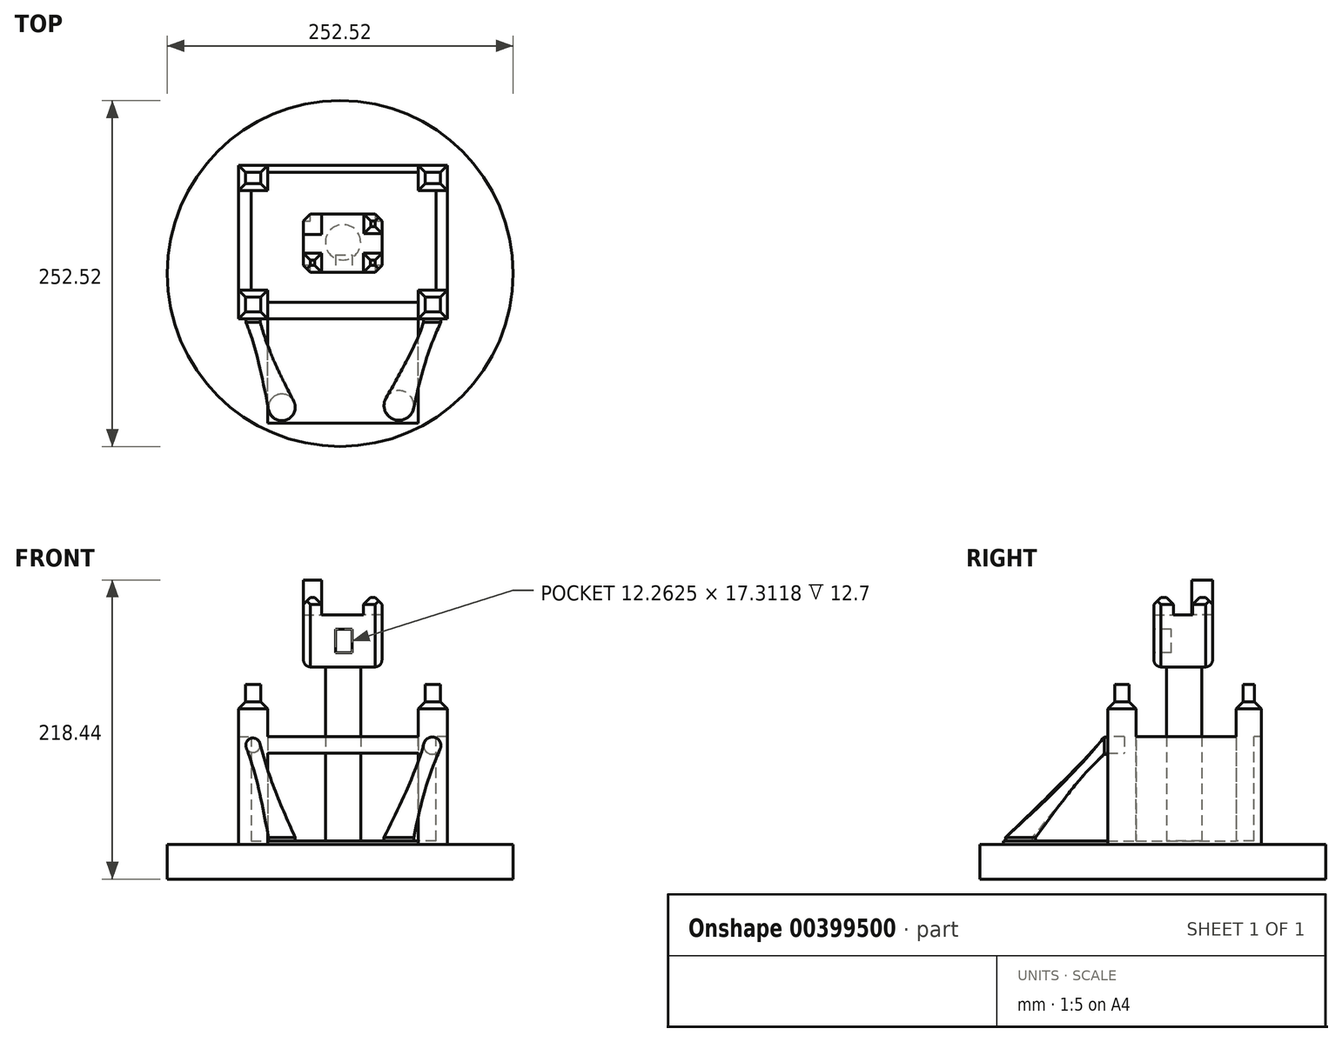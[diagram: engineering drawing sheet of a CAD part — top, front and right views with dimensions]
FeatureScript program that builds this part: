
annotation { "Feature Type Name" : "Feature", "Feature Type Description" : "" }
export const myFeature = defineFeature(function(context is Context, id is Id, definition is map)
    precondition{}
    {
        {
            var Q0;
            Q0=qCreatedBy(makeId("Top.planeOp"),FACE);
            var sketch = newSketch(context, id + "F0", { "sketchPlane" : qUnion([Q0])});
            skLineSegment(sketch, "E0.bottom", {"start": v(-76.3, 56.28) * mm, "end": v(76.12, 56.28) * mm});
            skLineSegment(sketch, "E0.top", {"start": v(-76.3, -55.71) * mm, "end": v(76.12, -55.71) * mm});
            skLineSegment(sketch, "E0.left", {"start": v(-76.3, 56.28) * mm, "end": v(-76.3, -55.71) * mm});
            skLineSegment(sketch, "E0.right", {"start": v(76.12, 56.28) * mm, "end": v(76.12, -55.71) * mm});
            skSolve(sketch);
        }
        {
            var Q0;
            Q0 = qSketchRegion(id + "F0", true);
            extrude(context, id + "F1", {"entities" : qUnion([Q0]), "depth" : 2.54 * mm});
        }
        {
            var Q0;
            Q0=makeQuery(id+"F1.opExtrude","CAP_FACE",FACE,{"disambiguationData":[OSD([sQuery(id+"F0.wireOp",EDGE,"E0.bottom"),sQuery(id+"F0.wireOp",EDGE,"E0.top"),sQuery(id+"F0.wireOp",EDGE,"E0.left"),sQuery(id+"F0.wireOp",EDGE,"E0.right")])],"isStart":false});
            var sketch = newSketch(context, id + "F2", { "sketchPlane" : qUnion([Q0])});
            skLineSegment(sketch, "E1.bottom", {"start": v(-76.3, 56.28) * mm, "end": v(-55.1, 56.28) * mm});
            skLineSegment(sketch, "E1.top", {"start": v(-76.3, 37.87) * mm, "end": v(-55.1, 37.87) * mm});
            skLineSegment(sketch, "E1.left", {"start": v(-76.3, 56.28) * mm, "end": v(-76.3, 37.87) * mm});
            skLineSegment(sketch, "E1.right", {"start": v(-55.1, 56.28) * mm, "end": v(-55.1, 37.87) * mm});
            skLineSegment(sketch, "E2.bottom", {"start": v(-76.3, -55.71) * mm, "end": v(-55.1, -55.71) * mm});
            skLineSegment(sketch, "E2.top", {"start": v(-76.3, -35.02) * mm, "end": v(-55.1, -35.02) * mm});
            skLineSegment(sketch, "E2.left", {"start": v(-76.3, -55.71) * mm, "end": v(-76.3, -35.02) * mm});
            skLineSegment(sketch, "E2.right", {"start": v(-55.1, -55.71) * mm, "end": v(-55.1, -35.02) * mm});
            skLineSegment(sketch, "E3.bottom", {"start": v(76.12, -55.71) * mm, "end": v(54.8, -55.71) * mm});
            skLineSegment(sketch, "E3.top", {"start": v(76.12, -35.02) * mm, "end": v(54.8, -35.02) * mm});
            skLineSegment(sketch, "E3.left", {"start": v(76.12, -55.71) * mm, "end": v(76.12, -35.02) * mm});
            skLineSegment(sketch, "E3.right", {"start": v(54.8, -55.71) * mm, "end": v(54.8, -35.02) * mm});
            skLineSegment(sketch, "E4.bottom", {"start": v(76.12, 56.28) * mm, "end": v(54.8, 56.28) * mm});
            skLineSegment(sketch, "E4.top", {"start": v(76.12, 37.87) * mm, "end": v(54.8, 37.87) * mm});
            skLineSegment(sketch, "E4.left", {"start": v(76.12, 56.28) * mm, "end": v(76.12, 37.87) * mm});
            skLineSegment(sketch, "E4.right", {"start": v(54.8, 56.28) * mm, "end": v(54.8, 37.87) * mm});
            skSolve(sketch);
        }
        {
            var Q0;
            Q0 = qSketchRegion(id + "F2", true);
            extrude(context, id + "F3", {"entities" : qUnion([Q0]), "operationType" : NewBodyOperationType.ADD, "depth" : 76.2 * mm});
        }
        {
            var Q0;
            Q0=makeQuery(id+"F3.opExtrude","SWEPT_FACE",FACE,{"disambiguationData":[OSD([sQuery(id+"F2.wireOp",EDGE,"E1.top")])]});
            var sketch = newSketch(context, id + "F4", { "sketchPlane" : qUnion([Q0])});
            skLineSegment(sketch, "E5.bottom", {"start": v(-76.3, 78.74) * mm, "end": v(-67.11, 78.74) * mm});
            skLineSegment(sketch, "E5.top", {"start": v(-76.3, 2.54) * mm, "end": v(-67.11, 2.54) * mm});
            skLineSegment(sketch, "E5.left", {"start": v(-76.3, 78.74) * mm, "end": v(-76.3, 2.54) * mm});
            skLineSegment(sketch, "E5.right", {"start": v(-67.11, 78.74) * mm, "end": v(-67.11, 2.54) * mm});
            skSolve(sketch);
        }
        {
            var Q0;
            Q0 = qSketchRegion(id + "F4", true);
            extrude(context, id + "F5", {"entities" : qUnion([Q0]), "operationType" : NewBodyOperationType.ADD, "depth" : 76.2 * mm});
        }
        {
            var Q0;
            Q0=makeQuery(id+"F3.opExtrude","SWEPT_FACE",FACE,{"disambiguationData":[OSD([sQuery(id+"F2.wireOp",EDGE,"E1.right")])]});
            var sketch = newSketch(context, id + "F6", { "sketchPlane" : qUnion([Q0])});
            skLineSegment(sketch, "E6.bottom", {"start": v(56.28, 78.74) * mm, "end": v(51.02, 78.74) * mm});
            skLineSegment(sketch, "E6.top", {"start": v(56.28, 2.54) * mm, "end": v(51.02, 2.54) * mm});
            skLineSegment(sketch, "E6.left", {"start": v(56.28, 78.74) * mm, "end": v(56.28, 2.54) * mm});
            skLineSegment(sketch, "E6.right", {"start": v(51.02, 78.74) * mm, "end": v(51.02, 2.54) * mm});
            skSolve(sketch);
        }
        {
            var Q0;
            Q0 = qSketchRegion(id + "F6", true);
            extrude(context, id + "F7", {"entities" : qUnion([Q0]), "operationType" : NewBodyOperationType.ADD, "depth" : 76.2 * mm});
        }
        {
            var Q0;
            Q0=makeQuery(id+"F7.opExtrude","CAP_FACE",FACE,{"disambiguationData":[OSD([sQuery(id+"F6.wireOp",EDGE,"E6.bottom"),sQuery(id+"F6.wireOp",EDGE,"E6.top"),sQuery(id+"F6.wireOp",EDGE,"E6.left"),sQuery(id+"F6.wireOp",EDGE,"E6.right")])],"isStart":false});
            var sketch = newSketch(context, id + "F8", { "sketchPlane" : qUnion([Q0])});
            skLineSegment(sketch, "E7.bottom", {"start": v(51.02, 78.74) * mm, "end": v(56.28, 78.74) * mm});
            skLineSegment(sketch, "E7.top", {"start": v(51.02, 2.54) * mm, "end": v(56.28, 2.54) * mm});
            skLineSegment(sketch, "E7.left", {"start": v(51.02, 78.74) * mm, "end": v(51.02, 2.54) * mm});
            skLineSegment(sketch, "E7.right", {"start": v(56.28, 78.74) * mm, "end": v(56.28, 2.54) * mm});
            skSolve(sketch);
        }
        {
            var Q0;
            Q0 = qSketchRegion(id + "F8", true);
            extrude(context, id + "F9", {"entities" : qUnion([Q0]), "operationType" : NewBodyOperationType.ADD, "depth" : 25.4 * mm});
        }
        {
            var Q0;
            Q0=makeQuery(id+"F9.opExtrude","CAP_FACE",FACE,{"disambiguationData":[OSD([sQuery(id+"F8.wireOp",EDGE,"E7.bottom"),sQuery(id+"F8.wireOp",EDGE,"E7.top"),sQuery(id+"F8.wireOp",EDGE,"E7.left"),sQuery(id+"F8.wireOp",EDGE,"E7.right")])],"isStart":false});
            var sketch = newSketch(context, id + "F10", { "sketchPlane" : qUnion([Q0])});
            skLineSegment(sketch, "E8.bottom", {"start": v(56.28, 78.74) * mm, "end": v(51.02, 78.74) * mm});
            skLineSegment(sketch, "E8.top", {"start": v(56.28, 2.54) * mm, "end": v(51.02, 2.54) * mm});
            skLineSegment(sketch, "E8.left", {"start": v(56.28, 78.74) * mm, "end": v(56.28, 2.54) * mm});
            skLineSegment(sketch, "E8.right", {"start": v(51.02, 78.74) * mm, "end": v(51.02, 2.54) * mm});
            skSolve(sketch);
        }
        {
            var Q0;
            Q0 = qSketchRegion(id + "F10", true);
            extrude(context, id + "F11", {"entities" : qUnion([Q0]), "operationType" : NewBodyOperationType.ADD, "depth" : 25.4 * mm});
        }
        {
            var Q0;
            Q0=makeQuery(id+"F3.opExtrude","SWEPT_FACE",FACE,{"disambiguationData":[OSD([sQuery(id+"F2.wireOp",EDGE,"E4.top")])]});
            var sketch = newSketch(context, id + "F12", { "sketchPlane" : qUnion([Q0])});
            skLineSegment(sketch, "E9.bottom", {"start": v(76.12, 78.74) * mm, "end": v(67.8, 78.74) * mm});
            skLineSegment(sketch, "E9.top", {"start": v(76.12, 2.54) * mm, "end": v(67.8, 2.54) * mm});
            skLineSegment(sketch, "E9.left", {"start": v(76.12, 78.74) * mm, "end": v(76.12, 2.54) * mm});
            skLineSegment(sketch, "E9.right", {"start": v(67.8, 78.74) * mm, "end": v(67.8, 2.54) * mm});
            skSolve(sketch);
        }
        {
            var Q0;
            Q0 = qSketchRegion(id + "F12", true);
            extrude(context, id + "F13", {"entities" : qUnion([Q0]), "operationType" : NewBodyOperationType.ADD, "depth" : 76.2 * mm});
        }
        {
            var Q0;
            Q0=makeQuery(id+"F3.opExtrude","SWEPT_FACE",FACE,{"disambiguationData":[OSD([sQuery(id+"F2.wireOp",EDGE,"E2.right")])]});
            var sketch = newSketch(context, id + "F14", { "sketchPlane" : qUnion([Q0])});
            skLineSegment(sketch, "E10.bottom", {"start": v(-55.71, 78.74) * mm, "end": v(-43.7, 78.74) * mm});
            skLineSegment(sketch, "E10.top", {"start": v(-55.71, 66.65) * mm, "end": v(-43.7, 66.65) * mm});
            skLineSegment(sketch, "E10.left", {"start": v(-55.71, 78.74) * mm, "end": v(-55.71, 66.65) * mm});
            skLineSegment(sketch, "E10.right", {"start": v(-43.7, 78.74) * mm, "end": v(-43.7, 66.65) * mm});
            skSolve(sketch);
        }
        {
            var Q0;
            Q0 = qSketchRegion(id + "F14", true);
            extrude(context, id + "F15", {"entities" : qUnion([Q0]), "operationType" : NewBodyOperationType.ADD, "depth" : 114.3 * mm});
        }
        {
            var Q0;
            Q0=makeQuery(id+"F15.boolean.opBoolean","MERGE",FACE,{"derivedFrom":[makeQuery(id+"F13.boolean.opBoolean","MERGE",FACE,{"derivedFrom":[makeQuery(id+"F3.opExtrude","CAP_FACE",FACE,{"disambiguationData":[OSD([sQuery(id+"F2.wireOp",EDGE,"E3.bottom"),sQuery(id+"F2.wireOp",EDGE,"E3.top"),sQuery(id+"F2.wireOp",EDGE,"E3.left"),sQuery(id+"F2.wireOp",EDGE,"E3.right")])],"isStart":false}),makeQuery(id+"F11.boolean.opBoolean","MERGE",FACE,{"derivedFrom":[makeQuery(id+"F3.opExtrude","CAP_FACE",FACE,{"disambiguationData":[OSD([sQuery(id+"F2.wireOp",EDGE,"E4.bottom"),sQuery(id+"F2.wireOp",EDGE,"E4.top"),sQuery(id+"F2.wireOp",EDGE,"E4.left"),sQuery(id+"F2.wireOp",EDGE,"E4.right")])],"isStart":false}),makeQuery(id+"F9.boolean.opBoolean","MERGE",FACE,{"derivedFrom":[makeQuery(id+"F7.boolean.opBoolean","MERGE",FACE,{"derivedFrom":[makeQuery(id+"F5.boolean.opBoolean","MERGE",FACE,{"derivedFrom":[makeQuery(id+"F3.opExtrude","CAP_FACE",FACE,{"disambiguationData":[OSD([sQuery(id+"F2.wireOp",EDGE,"E1.bottom"),sQuery(id+"F2.wireOp",EDGE,"E1.top"),sQuery(id+"F2.wireOp",EDGE,"E1.left"),sQuery(id+"F2.wireOp",EDGE,"E1.right")])],"isStart":false}),makeQuery(id+"F3.opExtrude","CAP_FACE",FACE,{"disambiguationData":[OSD([sQuery(id+"F2.wireOp",EDGE,"E2.bottom"),sQuery(id+"F2.wireOp",EDGE,"E2.top"),sQuery(id+"F2.wireOp",EDGE,"E2.left"),sQuery(id+"F2.wireOp",EDGE,"E2.right")])],"isStart":false}),makeQuery(id+"F5.opExtrude","SWEPT_FACE",FACE,{"disambiguationData":[OSD([sQuery(id+"F4.wireOp",EDGE,"E5.bottom")])]})]}),makeQuery(id+"F7.opExtrude","SWEPT_FACE",FACE,{"disambiguationData":[OSD([sQuery(id+"F6.wireOp",EDGE,"E6.bottom")])]})]}),makeQuery(id+"F9.opExtrude","SWEPT_FACE",FACE,{"disambiguationData":[OSD([sQuery(id+"F8.wireOp",EDGE,"E7.bottom")])]})]}),makeQuery(id+"F11.opExtrude","SWEPT_FACE",FACE,{"disambiguationData":[OSD([sQuery(id+"F10.wireOp",EDGE,"E8.bottom")])]})]}),makeQuery(id+"F13.opExtrude","SWEPT_FACE",FACE,{"disambiguationData":[OSD([sQuery(id+"F12.wireOp",EDGE,"E9.bottom")])]})]}),makeQuery(id+"F15.opExtrude","SWEPT_FACE",FACE,{"disambiguationData":[OSD([sQuery(id+"F14.wireOp",EDGE,"E10.bottom")])]})]});
            var sketch = newSketch(context, id + "F16", { "sketchPlane" : qUnion([Q0])});
            skLineSegment(sketch, "E11.bottom", {"start": v(54.8, -35.02) * mm, "end": v(76.12, -35.02) * mm});
            skLineSegment(sketch, "E11.top", {"start": v(54.8, -55.71) * mm, "end": v(76.12, -55.71) * mm});
            skLineSegment(sketch, "E11.left", {"start": v(54.8, -35.02) * mm, "end": v(54.8, -55.71) * mm});
            skLineSegment(sketch, "E11.right", {"start": v(76.12, -35.02) * mm, "end": v(76.12, -55.71) * mm});
            skLineSegment(sketch, "E12.bottom", {"start": v(54.8, 37.87) * mm, "end": v(76.12, 37.87) * mm});
            skLineSegment(sketch, "E12.top", {"start": v(54.8, 56.28) * mm, "end": v(76.12, 56.28) * mm});
            skLineSegment(sketch, "E12.left", {"start": v(54.8, 37.87) * mm, "end": v(54.8, 56.28) * mm});
            skLineSegment(sketch, "E12.right", {"start": v(76.12, 37.87) * mm, "end": v(76.12, 56.28) * mm});
            skLineSegment(sketch, "E13.bottom", {"start": v(-55.1, 37.87) * mm, "end": v(-76.3, 37.87) * mm});
            skLineSegment(sketch, "E13.top", {"start": v(-55.1, 56.28) * mm, "end": v(-76.3, 56.28) * mm});
            skLineSegment(sketch, "E13.left", {"start": v(-55.1, 37.87) * mm, "end": v(-55.1, 56.28) * mm});
            skLineSegment(sketch, "E13.right", {"start": v(-76.3, 37.87) * mm, "end": v(-76.3, 56.28) * mm});
            skLineSegment(sketch, "E14.bottom", {"start": v(-55.1, -35.02) * mm, "end": v(-76.3, -35.02) * mm});
            skLineSegment(sketch, "E14.top", {"start": v(-55.1, -55.71) * mm, "end": v(-76.3, -55.71) * mm});
            skLineSegment(sketch, "E14.left", {"start": v(-55.1, -35.02) * mm, "end": v(-55.1, -55.71) * mm});
            skLineSegment(sketch, "E14.right", {"start": v(-76.3, -35.02) * mm, "end": v(-76.3, -55.71) * mm});
            skSolve(sketch);
        }
        {
            var Q0;
            Q0 = qSketchRegion(id + "F16", true);
            extrude(context, id + "F17", {"entities" : qUnion([Q0]), "operationType" : NewBodyOperationType.ADD, "depth" : 25.4 * mm});
        }
        {
            var Q0;
            Q0=makeQuery(id+"F17.opExtrude","CAP_EDGE",EDGE,{"disambiguationData":[OSD([sQuery(id+"F16.wireOp",EDGE,"E14.left")])],"isStart":false});
            var Q1;
            Q1=makeQuery(id+"F17.opExtrude","CAP_EDGE",EDGE,{"disambiguationData":[OSD([sQuery(id+"F16.wireOp",EDGE,"E14.top")])],"isStart":false});
            var Q2;
            Q2=makeQuery(id+"F17.opExtrude","CAP_EDGE",EDGE,{"disambiguationData":[OSD([sQuery(id+"F16.wireOp",EDGE,"E14.right")])],"isStart":false});
            var Q3;
            Q3=makeQuery(id+"F17.opExtrude","CAP_EDGE",EDGE,{"disambiguationData":[OSD([sQuery(id+"F16.wireOp",EDGE,"E14.bottom")])],"isStart":false});
            var Q4;
            Q4=makeQuery(id+"F17.opExtrude","CAP_EDGE",EDGE,{"disambiguationData":[OSD([sQuery(id+"F16.wireOp",EDGE,"E11.right")])],"isStart":false});
            var Q5;
            Q5=makeQuery(id+"F17.opExtrude","CAP_EDGE",EDGE,{"disambiguationData":[OSD([sQuery(id+"F16.wireOp",EDGE,"E11.top")])],"isStart":false});
            var Q6;
            Q6=makeQuery(id+"F17.opExtrude","CAP_EDGE",EDGE,{"disambiguationData":[OSD([sQuery(id+"F16.wireOp",EDGE,"E11.left")])],"isStart":false});
            var Q7;
            Q7=makeQuery(id+"F17.opExtrude","CAP_EDGE",EDGE,{"disambiguationData":[OSD([sQuery(id+"F16.wireOp",EDGE,"E11.bottom")])],"isStart":false});
            var Q8;
            Q8=makeQuery(id+"F17.opExtrude","CAP_EDGE",EDGE,{"disambiguationData":[OSD([sQuery(id+"F16.wireOp",EDGE,"E13.bottom")])],"isStart":false});
            var Q9;
            Q9=makeQuery(id+"F17.opExtrude","CAP_EDGE",EDGE,{"disambiguationData":[OSD([sQuery(id+"F16.wireOp",EDGE,"E13.left")])],"isStart":false});
            var Q10;
            Q10=makeQuery(id+"F17.opExtrude","CAP_EDGE",EDGE,{"disambiguationData":[OSD([sQuery(id+"F16.wireOp",EDGE,"E12.bottom")])],"isStart":false});
            var Q11;
            Q11=makeQuery(id+"F17.opExtrude","CAP_EDGE",EDGE,{"disambiguationData":[OSD([sQuery(id+"F16.wireOp",EDGE,"E12.right")])],"isStart":false});
            var Q12;
            Q12=makeQuery(id+"F17.opExtrude","CAP_EDGE",EDGE,{"disambiguationData":[OSD([sQuery(id+"F16.wireOp",EDGE,"E12.top")])],"isStart":false});
            var Q13;
            Q13=makeQuery(id+"F17.opExtrude","CAP_EDGE",EDGE,{"disambiguationData":[OSD([sQuery(id+"F16.wireOp",EDGE,"E12.left")])],"isStart":false});
            var Q14;
            Q14=makeQuery(id+"F17.opExtrude","CAP_EDGE",EDGE,{"disambiguationData":[OSD([sQuery(id+"F16.wireOp",EDGE,"E13.top")])],"isStart":false});
            var Q15;
            Q15=makeQuery(id+"F17.opExtrude","CAP_EDGE",EDGE,{"disambiguationData":[OSD([sQuery(id+"F16.wireOp",EDGE,"E13.right")])],"isStart":false});
            chamfer(context, id + "F18", {"entities" : qUnion([Q0, Q1, Q2, Q3, Q4, Q5, Q6, Q7, Q8, Q9, Q10, Q11, Q12, Q13, Q14, Q15]), "width" : 5.08 * mm, "tangentPropagation" : true});
        }
        {
            var Q0;
            Q0=makeQuery(id+"F17.opExtrude","CAP_FACE",FACE,{"disambiguationData":[OSD([sQuery(id+"F16.wireOp",EDGE,"E11.bottom"),sQuery(id+"F16.wireOp",EDGE,"E11.top"),sQuery(id+"F16.wireOp",EDGE,"E11.left"),sQuery(id+"F16.wireOp",EDGE,"E11.right")])],"isStart":false});
            var sketch = newSketch(context, id + "F19", { "sketchPlane" : qUnion([Q0])});
            skLineSegment(sketch, "E15.bottom", {"start": v(59.88, -50.63) * mm, "end": v(71.04, -50.63) * mm});
            skLineSegment(sketch, "E15.top", {"start": v(59.88, -40.1) * mm, "end": v(71.04, -40.1) * mm});
            skLineSegment(sketch, "E15.left", {"start": v(59.88, -50.63) * mm, "end": v(59.88, -40.1) * mm});
            skLineSegment(sketch, "E15.right", {"start": v(71.04, -50.63) * mm, "end": v(71.04, -40.1) * mm});
            skSolve(sketch);
        }
        {
            var Q0;
            Q0 = qSketchRegion(id + "F19", true);
            extrude(context, id + "F20", {"entities" : qUnion([Q0]), "operationType" : NewBodyOperationType.ADD, "depth" : 12.7 * mm});
        }
        {
            var Q0;
            Q0=makeQuery(id+"F17.opExtrude","CAP_FACE",FACE,{"disambiguationData":[OSD([sQuery(id+"F16.wireOp",EDGE,"E14.bottom"),sQuery(id+"F16.wireOp",EDGE,"E14.top"),sQuery(id+"F16.wireOp",EDGE,"E14.left"),sQuery(id+"F16.wireOp",EDGE,"E14.right")])],"isStart":false});
            var sketch = newSketch(context, id + "F21", { "sketchPlane" : qUnion([Q0])});
            skLineSegment(sketch, "E16.bottom", {"start": v(-71.23, -40.1) * mm, "end": v(-60.18, -40.1) * mm});
            skLineSegment(sketch, "E16.top", {"start": v(-71.23, -50.63) * mm, "end": v(-60.18, -50.63) * mm});
            skLineSegment(sketch, "E16.left", {"start": v(-71.23, -40.1) * mm, "end": v(-71.23, -50.63) * mm});
            skLineSegment(sketch, "E16.right", {"start": v(-60.18, -40.1) * mm, "end": v(-60.18, -50.63) * mm});
            skSolve(sketch);
        }
        {
            var Q0;
            Q0 = qSketchRegion(id + "F21", true);
            extrude(context, id + "F22", {"entities" : qUnion([Q0]), "operationType" : NewBodyOperationType.ADD, "depth" : 12.7 * mm});
        }
        {
            var Q0;
            Q0=makeQuery(id+"F17.opExtrude","CAP_FACE",FACE,{"disambiguationData":[OSD([sQuery(id+"F16.wireOp",EDGE,"E13.bottom"),sQuery(id+"F16.wireOp",EDGE,"E13.top"),sQuery(id+"F16.wireOp",EDGE,"E13.left"),sQuery(id+"F16.wireOp",EDGE,"E13.right")])],"isStart":false});
            var sketch = newSketch(context, id + "F23", { "sketchPlane" : qUnion([Q0])});
            skLineSegment(sketch, "E17.bottom", {"start": v(-71.23, 51.2) * mm, "end": v(-60.18, 51.2) * mm});
            skLineSegment(sketch, "E17.top", {"start": v(-71.23, 42.95) * mm, "end": v(-60.18, 42.95) * mm});
            skLineSegment(sketch, "E17.left", {"start": v(-71.23, 51.2) * mm, "end": v(-71.23, 42.95) * mm});
            skLineSegment(sketch, "E17.right", {"start": v(-60.18, 51.2) * mm, "end": v(-60.18, 42.95) * mm});
            skSolve(sketch);
        }
        {
            var Q0;
            Q0 = qSketchRegion(id + "F23", true);
            extrude(context, id + "F24", {"entities" : qUnion([Q0]), "operationType" : NewBodyOperationType.ADD, "depth" : 12.7 * mm});
        }
        {
            var Q0;
            Q0=makeQuery(id+"F17.opExtrude","CAP_FACE",FACE,{"disambiguationData":[OSD([sQuery(id+"F16.wireOp",EDGE,"E12.bottom"),sQuery(id+"F16.wireOp",EDGE,"E12.top"),sQuery(id+"F16.wireOp",EDGE,"E12.left"),sQuery(id+"F16.wireOp",EDGE,"E12.right")])],"isStart":false});
            var sketch = newSketch(context, id + "F25", { "sketchPlane" : qUnion([Q0])});
            skLineSegment(sketch, "E18.bottom", {"start": v(59.88, 51.2) * mm, "end": v(71.04, 51.2) * mm});
            skLineSegment(sketch, "E18.top", {"start": v(59.88, 42.95) * mm, "end": v(71.04, 42.95) * mm});
            skLineSegment(sketch, "E18.left", {"start": v(59.88, 51.2) * mm, "end": v(59.88, 42.95) * mm});
            skLineSegment(sketch, "E18.right", {"start": v(71.04, 51.2) * mm, "end": v(71.04, 42.95) * mm});
            skSolve(sketch);
        }
        {
            var Q0;
            Q0 = qSketchRegion(id + "F25", true);
            extrude(context, id + "F26", {"entities" : qUnion([Q0]), "operationType" : NewBodyOperationType.ADD, "depth" : 12.7 * mm});
        }
        {
            var Q0;
            Q0=makeQuery(id+"F17.boolean.opBoolean","MERGE",FACE,{"derivedFrom":[makeQuery(id+"F15.boolean.opBoolean","MERGE",FACE,{"derivedFrom":[makeQuery(id+"F3.boolean.opBoolean","MERGE",FACE,{"derivedFrom":[makeQuery(id+"F1.opExtrude","SWEPT_FACE",FACE,{"disambiguationData":[OSD([sQuery(id+"F0.wireOp",EDGE,"E0.top")])]}),makeQuery(id+"F3.opExtrude","SWEPT_FACE",FACE,{"disambiguationData":[OSD([sQuery(id+"F2.wireOp",EDGE,"E2.bottom")])]}),makeQuery(id+"F3.opExtrude","SWEPT_FACE",FACE,{"disambiguationData":[OSD([sQuery(id+"F2.wireOp",EDGE,"E3.bottom")])]})]}),makeQuery(id+"F15.opExtrude","SWEPT_FACE",FACE,{"disambiguationData":[OSD([sQuery(id+"F14.wireOp",EDGE,"E10.left")])]})]}),makeQuery(id+"F17.opExtrude","SWEPT_FACE",FACE,{"disambiguationData":[OSD([sQuery(id+"F16.wireOp",EDGE,"E11.top")])]}),makeQuery(id+"F17.opExtrude","SWEPT_FACE",FACE,{"disambiguationData":[OSD([sQuery(id+"F16.wireOp",EDGE,"E14.top")])]})]});
            var sketch = newSketch(context, id + "F27", { "sketchPlane" : qUnion([Q0])});
            skLineSegment(sketch, "E19.bottom", {"start": v(-55.1, 2.54) * mm, "end": v(54.8, 2.54) * mm});
            skLineSegment(sketch, "E19.top", {"start": v(-55.1, 0) * mm, "end": v(54.8, 0) * mm});
            skLineSegment(sketch, "E19.left", {"start": v(-55.1, 2.54) * mm, "end": v(-55.1, 0) * mm});
            skLineSegment(sketch, "E19.right", {"start": v(54.8, 2.54) * mm, "end": v(54.8, 0) * mm});
            skSolve(sketch);
        }
        {
            var Q0;
            Q0 = qSketchRegion(id + "F27", true);
            extrude(context, id + "F28", {"entities" : qUnion([Q0]), "operationType" : NewBodyOperationType.ADD, "depth" : 76.2 * mm});
        }
        {
            var Q0;
            Q0=makeQuery(id+"F17.boolean.opBoolean","MERGE",FACE,{"derivedFrom":[makeQuery(id+"F15.boolean.opBoolean","MERGE",FACE,{"derivedFrom":[makeQuery(id+"F3.boolean.opBoolean","MERGE",FACE,{"derivedFrom":[makeQuery(id+"F1.opExtrude","SWEPT_FACE",FACE,{"disambiguationData":[OSD([sQuery(id+"F0.wireOp",EDGE,"E0.top")])]}),makeQuery(id+"F3.opExtrude","SWEPT_FACE",FACE,{"disambiguationData":[OSD([sQuery(id+"F2.wireOp",EDGE,"E2.bottom")])]}),makeQuery(id+"F3.opExtrude","SWEPT_FACE",FACE,{"disambiguationData":[OSD([sQuery(id+"F2.wireOp",EDGE,"E3.bottom")])]})]}),makeQuery(id+"F15.opExtrude","SWEPT_FACE",FACE,{"disambiguationData":[OSD([sQuery(id+"F14.wireOp",EDGE,"E10.left")])]})]}),makeQuery(id+"F17.opExtrude","SWEPT_FACE",FACE,{"disambiguationData":[OSD([sQuery(id+"F16.wireOp",EDGE,"E11.top")])]}),makeQuery(id+"F17.opExtrude","SWEPT_FACE",FACE,{"disambiguationData":[OSD([sQuery(id+"F16.wireOp",EDGE,"E14.top")])]})]});
            var sketch = newSketch(context, id + "F29", { "sketchPlane" : qUnion([Q0])});
            skCircle(sketch, "E20", {"center": v(65.16, 72.07) * mm, "radius": 6.69 * mm});
            skSolve(sketch);
        }
        {
            var Q0;
            Q0=makeQuery(id+"F28.boolean.opBoolean","MERGE",FACE,{"derivedFrom":[makeQuery(id+"F1.opExtrude","CAP_FACE",FACE,{"disambiguationData":[OSD([sQuery(id+"F0.wireOp",EDGE,"E0.bottom"),sQuery(id+"F0.wireOp",EDGE,"E0.top"),sQuery(id+"F0.wireOp",EDGE,"E0.left"),sQuery(id+"F0.wireOp",EDGE,"E0.right")])],"isStart":false}),makeQuery(id+"F28.opExtrude","SWEPT_FACE",FACE,{"disambiguationData":[OSD([sQuery(id+"F27.wireOp",EDGE,"E19.bottom")])]})]});
            var sketch = newSketch(context, id + "F30", { "sketchPlane" : qUnion([Q0])});
            skCircle(sketch, "E21", {"center": v(40.8, -119.14) * mm, "radius": 10.86 * mm});
            skSolve(sketch);
        }
        {
            var Q0;
            Q0 = qSketchRegion(id + "F30", true);
            extrude(context, id + "F31", {"entities" : qUnion([Q0]), "operationType" : NewBodyOperationType.ADD, "depth" : 2.54 * mm});
        }
        {
            var Q0;
            Q0=sQuery(id+"F29.wireOp",EDGE,"E20");
            extrude(context, id + "F32", {"bodyType" : ToolBodyType.SURFACE, "surfaceEntities" : qUnion([Q0]), "depth" : 2.54 * mm});
        }
        {
            var Q0;
            Q0=makeQuery(id+"F17.boolean.opBoolean","MERGE",FACE,{"derivedFrom":[makeQuery(id+"F15.boolean.opBoolean","MERGE",FACE,{"derivedFrom":[makeQuery(id+"F3.boolean.opBoolean","MERGE",FACE,{"derivedFrom":[makeQuery(id+"F1.opExtrude","SWEPT_FACE",FACE,{"disambiguationData":[OSD([sQuery(id+"F0.wireOp",EDGE,"E0.top")])]}),makeQuery(id+"F3.opExtrude","SWEPT_FACE",FACE,{"disambiguationData":[OSD([sQuery(id+"F2.wireOp",EDGE,"E2.bottom")])]}),makeQuery(id+"F3.opExtrude","SWEPT_FACE",FACE,{"disambiguationData":[OSD([sQuery(id+"F2.wireOp",EDGE,"E3.bottom")])]})]}),makeQuery(id+"F15.opExtrude","SWEPT_FACE",FACE,{"disambiguationData":[OSD([sQuery(id+"F14.wireOp",EDGE,"E10.left")])]})]}),makeQuery(id+"F17.opExtrude","SWEPT_FACE",FACE,{"disambiguationData":[OSD([sQuery(id+"F16.wireOp",EDGE,"E11.top")])]}),makeQuery(id+"F17.opExtrude","SWEPT_FACE",FACE,{"disambiguationData":[OSD([sQuery(id+"F16.wireOp",EDGE,"E14.top")])]})]});
            var sketch = newSketch(context, id + "F33", { "sketchPlane" : qUnion([Q0])});
            skCircle(sketch, "E22", {"center": v(65.14, 72.03) * mm, "radius": 6.28 * mm});
            skSolve(sketch);
        }
        {
            var Q0;
            Q0 = qSketchRegion(id + "F33", true);
            extrude(context, id + "F34", {"entities" : qUnion([Q0]), "operationType" : NewBodyOperationType.ADD, "depth" : 2.54 * mm});
        }
        {
            var Q0;
            Q0=makeQuery(id+"F31.opExtrude","CAP_FACE",FACE,{"disambiguationData":[OSD([sQuery(id+"F30.wireOp",EDGE,"E21")])],"isStart":false});
            var Q1;
            Q1=makeQuery(id+"F34.opExtrude","CAP_FACE",FACE,{"disambiguationData":[OSD([sQuery(id+"F33.wireOp",EDGE,"E22")])],"isStart":false});
            loft(context, id + "F35", {"sheetProfilesArray" : [{ "sheetProfileEntities" : qUnion([Q0]) }, { "sheetProfileEntities" : qUnion([Q1]) }]});
        }
        {
            var Q0;
            Q0=makeQuery(id+"F28.boolean.opBoolean","MERGE",FACE,{"derivedFrom":[makeQuery(id+"F1.opExtrude","CAP_FACE",FACE,{"disambiguationData":[OSD([sQuery(id+"F0.wireOp",EDGE,"E0.bottom"),sQuery(id+"F0.wireOp",EDGE,"E0.top"),sQuery(id+"F0.wireOp",EDGE,"E0.left"),sQuery(id+"F0.wireOp",EDGE,"E0.right")])],"isStart":false}),makeQuery(id+"F28.opExtrude","SWEPT_FACE",FACE,{"disambiguationData":[OSD([sQuery(id+"F27.wireOp",EDGE,"E19.bottom")])]})]});
            var sketch = newSketch(context, id + "F36", { "sketchPlane" : qUnion([Q0])});
            skCircle(sketch, "E23", {"center": v(-44.64, -120.53) * mm, "radius": 9.76 * mm});
            skSolve(sketch);
        }
        {
            var Q0;
            Q0 = qSketchRegion(id + "F36", true);
            extrude(context, id + "F37", {"entities" : qUnion([Q0]), "operationType" : NewBodyOperationType.ADD, "depth" : 2.54 * mm});
        }
        {
            var Q0;
            Q0=makeQuery(id+"F17.boolean.opBoolean","MERGE",FACE,{"derivedFrom":[makeQuery(id+"F15.boolean.opBoolean","MERGE",FACE,{"derivedFrom":[makeQuery(id+"F3.boolean.opBoolean","MERGE",FACE,{"derivedFrom":[makeQuery(id+"F1.opExtrude","SWEPT_FACE",FACE,{"disambiguationData":[OSD([sQuery(id+"F0.wireOp",EDGE,"E0.top")])]}),makeQuery(id+"F3.opExtrude","SWEPT_FACE",FACE,{"disambiguationData":[OSD([sQuery(id+"F2.wireOp",EDGE,"E2.bottom")])]}),makeQuery(id+"F3.opExtrude","SWEPT_FACE",FACE,{"disambiguationData":[OSD([sQuery(id+"F2.wireOp",EDGE,"E3.bottom")])]})]}),makeQuery(id+"F15.opExtrude","SWEPT_FACE",FACE,{"disambiguationData":[OSD([sQuery(id+"F14.wireOp",EDGE,"E10.left")])]})]}),makeQuery(id+"F17.opExtrude","SWEPT_FACE",FACE,{"disambiguationData":[OSD([sQuery(id+"F16.wireOp",EDGE,"E11.top")])]}),makeQuery(id+"F17.opExtrude","SWEPT_FACE",FACE,{"disambiguationData":[OSD([sQuery(id+"F16.wireOp",EDGE,"E14.top")])]})]});
            var sketch = newSketch(context, id + "F38", { "sketchPlane" : qUnion([Q0])});
            skCircle(sketch, "E24", {"center": v(-65.69, 72.32) * mm, "radius": 5.25 * mm});
            skSolve(sketch);
        }
        {
            var Q0;
            Q0 = qSketchRegion(id + "F38", true);
            extrude(context, id + "F39", {"entities" : qUnion([Q0]), "operationType" : NewBodyOperationType.ADD, "depth" : 2.54 * mm});
        }
        {
            var Q0;
            Q0=makeQuery(id+"F37.opExtrude","CAP_FACE",FACE,{"disambiguationData":[OSD([sQuery(id+"F36.wireOp",EDGE,"E23")])],"isStart":false});
            var Q1;
            Q1=makeQuery(id+"F39.opExtrude","CAP_FACE",FACE,{"disambiguationData":[OSD([sQuery(id+"F38.wireOp",EDGE,"E24")])],"isStart":false});
            loft(context, id + "F40", {"sheetProfilesArray" : [{ "sheetProfileEntities" : qUnion([Q0]) }, { "sheetProfileEntities" : qUnion([Q1]) }]});
        }
        {
            var Q0;
            Q0=makeQuery(id+"F28.boolean.opBoolean","MERGE",FACE,{"derivedFrom":[makeQuery(id+"F1.opExtrude","CAP_FACE",FACE,{"disambiguationData":[OSD([sQuery(id+"F0.wireOp",EDGE,"E0.bottom"),sQuery(id+"F0.wireOp",EDGE,"E0.top"),sQuery(id+"F0.wireOp",EDGE,"E0.left"),sQuery(id+"F0.wireOp",EDGE,"E0.right")])],"isStart":true}),makeQuery(id+"F28.opExtrude","SWEPT_FACE",FACE,{"disambiguationData":[OSD([sQuery(id+"F27.wireOp",EDGE,"E19.top")])]})]});
            var sketch = newSketch(context, id + "F41", { "sketchPlane" : qUnion([Q0])});
            skCircle(sketch, "E25", {"center": v(-2.13, 22.8) * mm, "radius": 126.26 * mm});
            skSolve(sketch);
        }
        {
            var Q0;
            Q0 = qSketchRegion(id + "F41", true);
            extrude(context, id + "F42", {"entities" : qUnion([Q0]), "operationType" : NewBodyOperationType.ADD, "depth" : 25.4 * mm});
        }
        {
            var Q0;
            Q0=makeQuery(id+"F28.boolean.opBoolean","MERGE",FACE,{"derivedFrom":[makeQuery(id+"F1.opExtrude","CAP_FACE",FACE,{"disambiguationData":[OSD([sQuery(id+"F0.wireOp",EDGE,"E0.bottom"),sQuery(id+"F0.wireOp",EDGE,"E0.top"),sQuery(id+"F0.wireOp",EDGE,"E0.left"),sQuery(id+"F0.wireOp",EDGE,"E0.right")])],"isStart":false}),makeQuery(id+"F28.opExtrude","SWEPT_FACE",FACE,{"disambiguationData":[OSD([sQuery(id+"F27.wireOp",EDGE,"E19.bottom")])]})]});
            var sketch = newSketch(context, id + "F43", { "sketchPlane" : qUnion([Q0])});
            skCircle(sketch, "E26", {"center": v(0, 0) * mm, "radius": 12.88 * mm});
            skSolve(sketch);
        }
        {
            var Q0;
            Q0 = qSketchRegion(id + "F43", true);
            extrude(context, id + "F44", {"entities" : qUnion([Q0]), "operationType" : NewBodyOperationType.ADD, "depth" : 127 * mm});
        }
        {
            var Q0;
            Q0=makeQuery(id+"F44.opExtrude","CAP_FACE",FACE,{"disambiguationData":[OSD([sQuery(id+"F43.wireOp",EDGE,"E26")])],"isStart":false});
            var sketch = newSketch(context, id + "F45", { "sketchPlane" : qUnion([Q0])});
            skLineSegment(sketch, "E27.bottom", {"start": v(-28.86, 20.76) * mm, "end": v(28.38, 20.76) * mm});
            skLineSegment(sketch, "E27.top", {"start": v(-28.86, -22.02) * mm, "end": v(28.38, -22.02) * mm});
            skLineSegment(sketch, "E27.left", {"start": v(-28.86, 20.76) * mm, "end": v(-28.86, -22.02) * mm});
            skLineSegment(sketch, "E27.right", {"start": v(28.38, 20.76) * mm, "end": v(28.38, -22.02) * mm});
            skSolve(sketch);
        }
        {
            var Q0;
            Q0 = qSketchRegion(id + "F45", true);
            extrude(context, id + "F46", {"entities" : qUnion([Q0]), "operationType" : NewBodyOperationType.ADD, "depth" : 38.1 * mm});
        }
        {
            var Q0;
            Q0=makeQuery(id+"F46.opExtrude","SWEPT_FACE",FACE,{"disambiguationData":[OSD([sQuery(id+"F45.wireOp",EDGE,"E27.top")])]});
            var sketch = newSketch(context, id + "F47", { "sketchPlane" : qUnion([Q0])});
            skLineSegment(sketch, "E28.bottom", {"start": v(-5.5, 139.77) * mm, "end": v(6.77, 139.77) * mm});
            skLineSegment(sketch, "E28.top", {"start": v(-5.5, 157.08) * mm, "end": v(6.77, 157.08) * mm});
            skLineSegment(sketch, "E28.left", {"start": v(-5.5, 139.77) * mm, "end": v(-5.5, 157.08) * mm});
            skLineSegment(sketch, "E28.right", {"start": v(6.77, 139.77) * mm, "end": v(6.77, 157.08) * mm});
            skSolve(sketch);
        }
        {
            var Q0;
            Q0 = qSketchRegion(id + "F47", true);
            extrude(context, id + "F48", {"entities" : qUnion([Q0]), "operationType" : NewBodyOperationType.REMOVE, "oppositeDirection" : true, "depth" : 12.7 * mm});
        }
        {
            var Q0;
            Q0=makeQuery(id+"F46.opExtrude","CAP_FACE",FACE,{"disambiguationData":[OSD([sQuery(id+"F45.wireOp",EDGE,"E27.bottom"),sQuery(id+"F45.wireOp",EDGE,"E27.top"),sQuery(id+"F45.wireOp",EDGE,"E27.left"),sQuery(id+"F45.wireOp",EDGE,"E27.right")])],"isStart":false});
            var sketch = newSketch(context, id + "F49", { "sketchPlane" : qUnion([Q0])});
            skLineSegment(sketch, "E29.bottom", {"start": v(28.38, 20.76) * mm, "end": v(15.17, 20.76) * mm});
            skLineSegment(sketch, "E29.top", {"start": v(28.38, 6.3) * mm, "end": v(15.17, 6.3) * mm});
            skLineSegment(sketch, "E29.left", {"start": v(28.38, 20.76) * mm, "end": v(28.38, 6.3) * mm});
            skLineSegment(sketch, "E29.right", {"start": v(15.17, 20.76) * mm, "end": v(15.17, 6.3) * mm});
            skLineSegment(sketch, "E30.bottom", {"start": v(28.38, -22.02) * mm, "end": v(14.86, -22.02) * mm});
            skLineSegment(sketch, "E30.top", {"start": v(28.38, -7.86) * mm, "end": v(14.86, -7.86) * mm});
            skLineSegment(sketch, "E30.left", {"start": v(28.38, -22.02) * mm, "end": v(28.38, -7.86) * mm});
            skLineSegment(sketch, "E30.right", {"start": v(14.86, -22.02) * mm, "end": v(14.86, -7.86) * mm});
            skLineSegment(sketch, "E31.bottom", {"start": v(-28.86, -22.02) * mm, "end": v(-15.65, -22.02) * mm});
            skLineSegment(sketch, "E31.top", {"start": v(-28.86, -7.86) * mm, "end": v(-15.65, -7.86) * mm});
            skLineSegment(sketch, "E31.left", {"start": v(-28.86, -22.02) * mm, "end": v(-28.86, -7.86) * mm});
            skLineSegment(sketch, "E31.right", {"start": v(-15.65, -22.02) * mm, "end": v(-15.65, -7.86) * mm});
            skLineSegment(sketch, "E32.bottom", {"start": v(-28.86, 20.76) * mm, "end": v(-15.65, 20.76) * mm});
            skLineSegment(sketch, "E32.top", {"start": v(-28.86, 5.66) * mm, "end": v(-15.65, 5.66) * mm});
            skLineSegment(sketch, "E32.left", {"start": v(-28.86, 20.76) * mm, "end": v(-28.86, 5.66) * mm});
            skLineSegment(sketch, "E32.right", {"start": v(-15.65, 20.76) * mm, "end": v(-15.65, 5.66) * mm});
            skSolve(sketch);
        }
        {
            var Q0;
            Q0 = qSketchRegion(id + "F49", true);
            extrude(context, id + "F50", {"entities" : qUnion([Q0]), "operationType" : NewBodyOperationType.ADD, "depth" : 25.4 * mm});
        }
        {
            var Q0;
            Q0=makeQuery(id+"F50.opExtrude","CAP_FACE",FACE,{"disambiguationData":[OSD([sQuery(id+"F49.wireOp",EDGE,"E32.bottom"),sQuery(id+"F49.wireOp",EDGE,"E32.top"),sQuery(id+"F49.wireOp",EDGE,"E32.left"),sQuery(id+"F49.wireOp",EDGE,"E32.right")])],"isStart":false});
            var sketch = newSketch(context, id + "F51", { "sketchPlane" : qUnion([Q0])});
            skSolve(sketch);
        }
        {
            var Q0;
            Q0=makeQuery(id+"F51.imprint","IMPRINT",FACE,{"disambiguationData":[TD([[makeQuery(id+"F51.imprint","IMPRINT",EDGE,{"derivedFrom":makeQuery(id+"F50.opExtrude","CAP_EDGE",EDGE,{"disambiguationData":[OSD([sQuery(id+"F49.wireOp",EDGE,"E32.bottom")])],"isStart":false})}),-1.0]])]});
            var Q1;
            Q1=makeQuery(id+"F50.opExtrude","CAP_FACE",FACE,{"disambiguationData":[OSD([sQuery(id+"F49.wireOp",EDGE,"E31.bottom"),sQuery(id+"F49.wireOp",EDGE,"E31.top"),sQuery(id+"F49.wireOp",EDGE,"E31.left"),sQuery(id+"F49.wireOp",EDGE,"E31.right")])],"isStart":false});
            var Q2;
            Q2=makeQuery(id+"F50.opExtrude","CAP_FACE",FACE,{"disambiguationData":[OSD([sQuery(id+"F49.wireOp",EDGE,"E30.bottom"),sQuery(id+"F49.wireOp",EDGE,"E30.top"),sQuery(id+"F49.wireOp",EDGE,"E30.left"),sQuery(id+"F49.wireOp",EDGE,"E30.right")])],"isStart":false});
            var Q3;
            Q3=makeQuery(id+"F50.opExtrude","CAP_FACE",FACE,{"disambiguationData":[OSD([sQuery(id+"F49.wireOp",EDGE,"E29.bottom"),sQuery(id+"F49.wireOp",EDGE,"E29.top"),sQuery(id+"F49.wireOp",EDGE,"E29.left"),sQuery(id+"F49.wireOp",EDGE,"E29.right")])],"isStart":false});
            extrude(context, id + "F52", {"entities" : qUnion([Q0, Q1, Q2, Q3]), "operationType" : NewBodyOperationType.REMOVE, "oppositeDirection" : true, "depth" : 12.7 * mm});
        }
        {
            var Q0;
            Q0=makeQuery(id+"F52.boolean.opBoolean","COPY",FACE,{"derivedFrom":makeQuery(id+"F52.opExtrude","CAP_FACE",FACE,{"disambiguationData":[OSD([sQuery(id+"F49.wireOp",EDGE,"E32.bottom"),sQuery(id+"F49.wireOp",EDGE,"E32.top"),sQuery(id+"F49.wireOp",EDGE,"E32.left"),sQuery(id+"F49.wireOp",EDGE,"E32.right")])],"isStart":false})});
            var Q1;
            Q1=makeQuery(id+"F52.boolean.opBoolean","COPY",FACE,{"derivedFrom":makeQuery(id+"F52.opExtrude","CAP_FACE",FACE,{"disambiguationData":[OSD([sQuery(id+"F49.wireOp",EDGE,"E31.bottom"),sQuery(id+"F49.wireOp",EDGE,"E31.top"),sQuery(id+"F49.wireOp",EDGE,"E31.left"),sQuery(id+"F49.wireOp",EDGE,"E31.right")])],"isStart":false})});
            var Q2;
            Q2=makeQuery(id+"F52.boolean.opBoolean","COPY",FACE,{"derivedFrom":makeQuery(id+"F52.opExtrude","CAP_FACE",FACE,{"disambiguationData":[OSD([sQuery(id+"F49.wireOp",EDGE,"E30.bottom"),sQuery(id+"F49.wireOp",EDGE,"E30.top"),sQuery(id+"F49.wireOp",EDGE,"E30.left"),sQuery(id+"F49.wireOp",EDGE,"E30.right")])],"isStart":false})});
            var Q3;
            Q3=makeQuery(id+"F52.boolean.opBoolean","COPY",FACE,{"derivedFrom":makeQuery(id+"F52.opExtrude","CAP_FACE",FACE,{"disambiguationData":[OSD([sQuery(id+"F49.wireOp",EDGE,"E29.bottom"),sQuery(id+"F49.wireOp",EDGE,"E29.top"),sQuery(id+"F49.wireOp",EDGE,"E29.left"),sQuery(id+"F49.wireOp",EDGE,"E29.right")])],"isStart":false})});
            chamfer(context, id + "F53", {"entities" : qUnion([Q0, Q1, Q2, Q3]), "width" : 5.08 * mm, "tangentPropagation" : true});
        }
        {
            var Q0;
            Q0=makeQuery(id+"F46.opExtrude","CAP_EDGE",EDGE,{"disambiguationData":[OSD([sQuery(id+"F45.wireOp",EDGE,"E27.top")])],"isStart":true});
            var Q1;
            Q1=makeQuery(id+"F46.opExtrude","CAP_EDGE",EDGE,{"disambiguationData":[OSD([sQuery(id+"F45.wireOp",EDGE,"E27.left")])],"isStart":true});
            var Q2;
            Q2=makeQuery(id+"F46.opExtrude","CAP_EDGE",EDGE,{"disambiguationData":[OSD([sQuery(id+"F45.wireOp",EDGE,"E27.bottom")])],"isStart":true});
            var Q3;
            Q3=makeQuery(id+"F46.opExtrude","CAP_EDGE",EDGE,{"disambiguationData":[OSD([sQuery(id+"F45.wireOp",EDGE,"E27.right")])],"isStart":true});
            fillet(context, id + "F54", {"entities" : qUnion([Q0, Q1, Q2, Q3]), "radius" : 5.08 * mm, "tangentPropagation" : true, "allowEdgeOverflow" : false});
        }
        {
            var Q0;
            Q0=makeQuery(id+"F50.boolean.opBoolean","MERGE",EDGE,{"derivedFrom":[makeQuery(id+"F46.opExtrude","SWEPT_EDGE",EDGE,{"disambiguationData":[OSD([sQuery(id+"F45.wireOp",EDGE,"E27.top"),sQuery(id+"F45.wireOp",EDGE,"E27.left")])]}),makeQuery(id+"F50.opExtrude","SWEPT_EDGE",EDGE,{"disambiguationData":[OSD([sQuery(id+"F49.wireOp",EDGE,"E31.bottom"),sQuery(id+"F49.wireOp",EDGE,"E31.left")])]})]});
            var Q1;
            Q1=makeQuery(id+"F50.boolean.opBoolean","MERGE",EDGE,{"derivedFrom":[makeQuery(id+"F46.opExtrude","SWEPT_EDGE",EDGE,{"disambiguationData":[OSD([sQuery(id+"F45.wireOp",EDGE,"E27.bottom"),sQuery(id+"F45.wireOp",EDGE,"E27.left")])]}),makeQuery(id+"F50.opExtrude","SWEPT_EDGE",EDGE,{"disambiguationData":[OSD([sQuery(id+"F49.wireOp",EDGE,"E32.bottom"),sQuery(id+"F49.wireOp",EDGE,"E32.left")])]})]});
            var Q2;
            Q2=makeQuery(id+"F50.boolean.opBoolean","MERGE",EDGE,{"derivedFrom":[makeQuery(id+"F46.opExtrude","SWEPT_EDGE",EDGE,{"disambiguationData":[OSD([sQuery(id+"F45.wireOp",EDGE,"E27.bottom"),sQuery(id+"F45.wireOp",EDGE,"E27.right")])]}),makeQuery(id+"F50.opExtrude","SWEPT_EDGE",EDGE,{"disambiguationData":[OSD([sQuery(id+"F49.wireOp",EDGE,"E29.bottom"),sQuery(id+"F49.wireOp",EDGE,"E29.left")])]})]});
            var Q3;
            Q3=makeQuery(id+"F50.boolean.opBoolean","MERGE",EDGE,{"derivedFrom":[makeQuery(id+"F46.opExtrude","SWEPT_EDGE",EDGE,{"disambiguationData":[OSD([sQuery(id+"F45.wireOp",EDGE,"E27.top"),sQuery(id+"F45.wireOp",EDGE,"E27.right")])]}),makeQuery(id+"F50.opExtrude","SWEPT_EDGE",EDGE,{"disambiguationData":[OSD([sQuery(id+"F49.wireOp",EDGE,"E30.bottom"),sQuery(id+"F49.wireOp",EDGE,"E30.left")])]})]});
            chamfer(context, id + "F55", {"entities" : qUnion([Q0, Q1, Q2, Q3]), "width" : 5.08 * mm, "tangentPropagation" : true});
        }
    });
